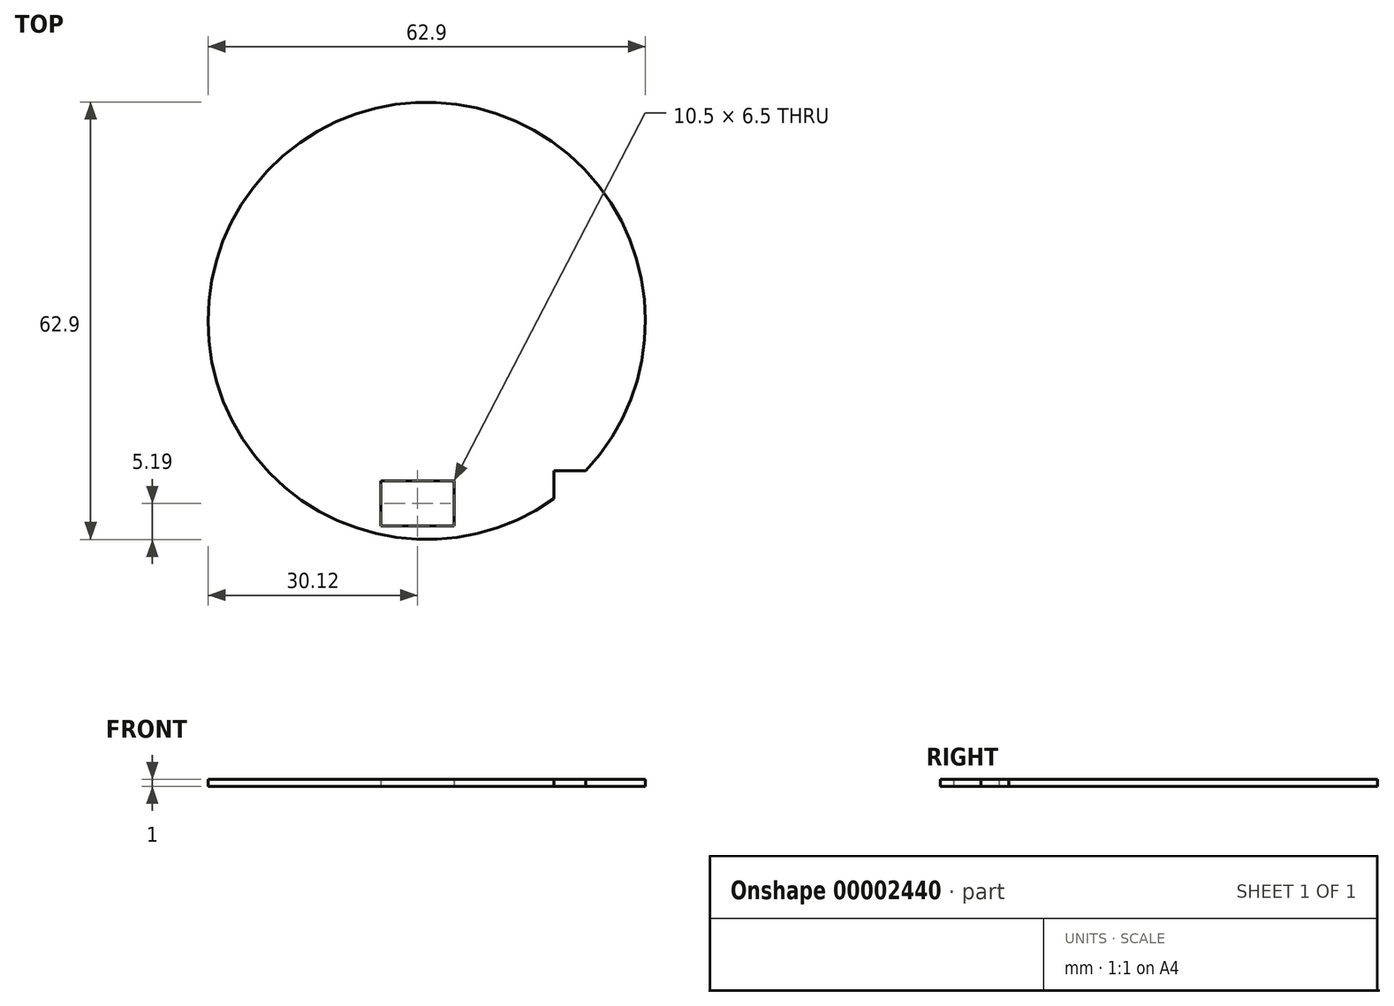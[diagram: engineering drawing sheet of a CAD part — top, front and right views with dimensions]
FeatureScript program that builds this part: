
annotation { "Feature Type Name" : "Feature", "Feature Type Description" : "" }
export const myFeature = defineFeature(function(context is Context, id is Id, definition is map)
    precondition{}
    {
        {
            var Q0;
            Q0=qCreatedBy(makeId("Top.planeOp"),FACE);
            var sketch = newSketch(context, id + "F0", { "sketchPlane" : qUnion([Q0])});
            skCircle(sketch, "E0", {"center": v(0, 0) * mm, "radius": 31.45 * mm});
            skLineSegment(sketch, "E1", {"start": v(0, 0) * mm, "end": v(0, -31.45) * mm, "construction": true});
            skLineSegment(sketch, "E2", {"start": v(6.42, -30.79) * mm, "end": v(6.42, -21.58) * mm, "construction": true});
            skLineSegment(sketch, "E3", {"start": v(6.42, -21.58) * mm, "end": v(22.88, -21.58) * mm, "construction": true});
            skLineSegment(sketch, "E4", {"start": v(3.92, -23) * mm, "end": v(3.92, -29.51) * mm});
            skLineSegment(sketch, "E5", {"start": v(3.92, -29.51) * mm, "end": v(-6.58, -29.51) * mm});
            skLineSegment(sketch, "E6", {"start": v(-6.58, -29.51) * mm, "end": v(-6.58, -23) * mm});
            skLineSegment(sketch, "E7", {"start": v(-6.58, -23) * mm, "end": v(3.92, -23) * mm});
            skLineSegment(sketch, "E8", {"start": v(-41.26, -31.45) * mm, "end": v(42.74, -31.45) * mm, "construction": true});
            skLineSegment(sketch, "E9", {"start": v(44.65, -21.58) * mm, "end": v(-50.65, -21.58) * mm, "construction": true});
            skLineSegment(sketch, "E10", {"start": v(18.3, -25.58) * mm, "end": v(18.3, -21.58) * mm});
            skLineSegment(sketch, "E11", {"start": v(18.3, -21.58) * mm, "end": v(22.88, -21.58) * mm});
            skSolve(sketch);
        }
        {
            var Q0;
            Q0=makeQuery(id+"F0.imprint","IMPRINT",FACE,{"disambiguationData":[TD([[makeQuery(id+"F0.imprint","IMPRINT",EDGE,{"derivedFrom":sQuery(id+"F0.wireOp",EDGE,"E4")}),1.0]])]});
            extrude(context, id + "F1", {"entities" : qUnion([Q0]), "depth" : 1 * mm});
        }
    });
